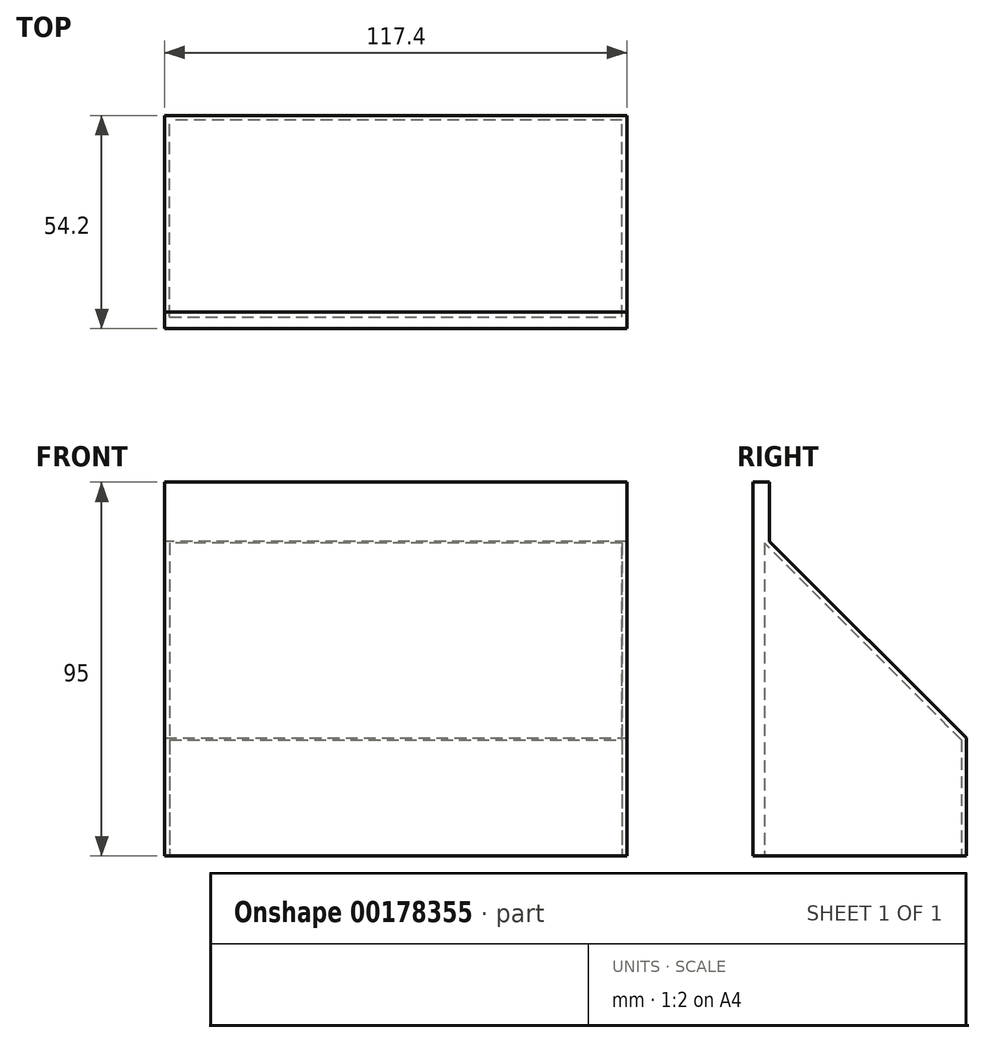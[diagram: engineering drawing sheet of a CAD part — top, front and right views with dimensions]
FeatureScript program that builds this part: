
annotation { "Feature Type Name" : "Feature", "Feature Type Description" : "" }
export const myFeature = defineFeature(function(context is Context, id is Id, definition is map)
    precondition{}
    {
        {
            var Q0;
            Q0=qCreatedBy(makeId("Top.planeOp"),FACE);
            var sketch = newSketch(context, id + "F0", { "sketchPlane" : qUnion([Q0])});
            skLineSegment(sketch, "E0.bottom", {"start": v(57.5, -25) * mm, "end": v(-57.5, -25) * mm});
            skLineSegment(sketch, "E0.top", {"start": v(57.5, 25) * mm, "end": v(-57.5, 25) * mm});
            skLineSegment(sketch, "E0.left", {"start": v(57.5, -25) * mm, "end": v(57.5, 25) * mm});
            skLineSegment(sketch, "E0.right", {"start": v(-57.5, -25) * mm, "end": v(-57.5, 25) * mm});
            skPoint(sketch, "E0.middle", {"position": v(0, 0) * mm});
            skLineSegment(sketch, "E1.0", {"start": v(58.7, -25) * mm, "end": v(58.7, 26.2) * mm});
            skLineSegment(sketch, "E1.1", {"start": v(58.7, 26.2) * mm, "end": v(-58.7, 26.2) * mm});
            skLineSegment(sketch, "E1.2", {"start": v(-58.7, -25) * mm, "end": v(-58.7, 26.2) * mm});
            skLineSegment(sketch, "E2.0", {"start": v(57.5, -28) * mm, "end": v(-57.5, -28) * mm});
            skLineSegment(sketch, "E3", {"start": v(-58.7, -25) * mm, "end": v(-58.7, -28) * mm});
            skLineSegment(sketch, "E4", {"start": v(-58.7, -28) * mm, "end": v(-57.5, -28) * mm});
            skLineSegment(sketch, "E5", {"start": v(58.7, -25) * mm, "end": v(58.7, -28) * mm});
            skLineSegment(sketch, "E6", {"start": v(58.7, -28) * mm, "end": v(57.5, -28) * mm});
            skSolve(sketch);
        }
        {
            var Q0;
            Q0 = qSketchRegion(id + "F0", true);
            var Q1;
            Q1=makeQuery(id+"F0.imprint","IMPRINT",FACE,{"disambiguationData":[TD([[makeQuery(id+"F0.imprint","IMPRINT",EDGE,{"derivedFrom":sQuery(id+"F0.wireOp",EDGE,"E0.bottom")}),-1.0]])]});
            extrude(context, id + "F1", {"entities" : qUnion([Q0, Q1]), "depth" : 80 * mm});
        }
        {
            var Q0;
            Q0=makeQuery(id+"F1.opExtrude","CAP_EDGE",EDGE,{"disambiguationData":[OSD([sQuery(id+"F0.wireOp",EDGE,"E1.1")])],"isStart":false});
            chamfer(context, id + "F2", {"entities" : qUnion([Q0]), "width" : 50 * mm, "tangentPropagation" : true});
        }
        {
            var Q0;
            Q0=makeQuery(id+"F1.opExtrude","CAP_FACE",FACE,{"disambiguationData":[OSD([sQuery(id+"F0.wireOp",EDGE,"E1.0"),sQuery(id+"F0.wireOp",EDGE,"E1.1"),sQuery(id+"F0.wireOp",EDGE,"E1.2"),sQuery(id+"F0.wireOp",EDGE,"E2.0"),sQuery(id+"F0.wireOp",EDGE,"E3"),sQuery(id+"F0.wireOp",EDGE,"E4"),sQuery(id+"F0.wireOp",EDGE,"E5"),sQuery(id+"F0.wireOp",EDGE,"E6")])],"isStart":false});
            extrude(context, id + "F3", {"entities" : qUnion([Q0]), "operationType" : NewBodyOperationType.ADD, "depth" : 15 * mm});
        }
        {
            var Q0;
            Q0=makeQuery(id+"F1.opExtrude","CAP_FACE",FACE,{"disambiguationData":[OSD([sQuery(id+"F0.wireOp",EDGE,"E1.0"),sQuery(id+"F0.wireOp",EDGE,"E1.1"),sQuery(id+"F0.wireOp",EDGE,"E1.2"),sQuery(id+"F0.wireOp",EDGE,"E2.0"),sQuery(id+"F0.wireOp",EDGE,"E3"),sQuery(id+"F0.wireOp",EDGE,"E4"),sQuery(id+"F0.wireOp",EDGE,"E5"),sQuery(id+"F0.wireOp",EDGE,"E6")])],"isStart":true});
            shell(context, id + "F4", {"entities" : qUnion([Q0]), "thickness" : 1.2 * mm});
        }
        {
            var Q0;
            Q0=makeQuery(id+"F4.opShell","OFFSET_FACE",FACE,{"disambiguationData":[OSD([sQuery(id+"F0.wireOp",EDGE,"E2.0"),sQuery(id+"F0.wireOp",EDGE,"E4"),sQuery(id+"F0.wireOp",EDGE,"E6")])]});
            extrude(context, id + "F5", {"entities" : qUnion([Q0]), "operationType" : NewBodyOperationType.ADD, "depth" : 1.8 * mm});
        }
    });
